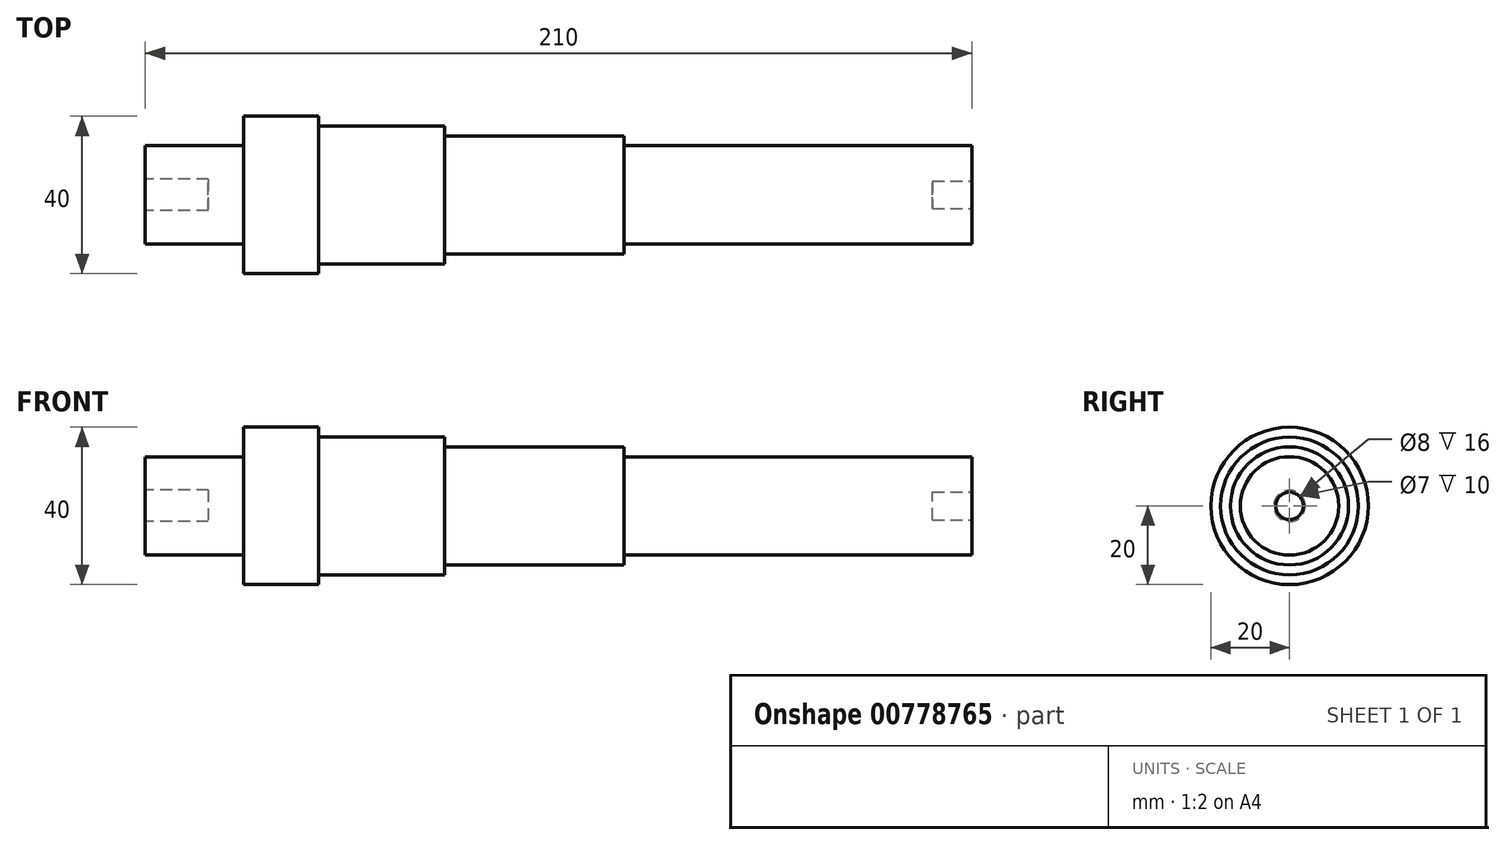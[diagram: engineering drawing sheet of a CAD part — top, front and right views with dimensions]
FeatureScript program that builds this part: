
annotation { "Feature Type Name" : "Feature", "Feature Type Description" : "" }
export const myFeature = defineFeature(function(context is Context, id is Id, definition is map)
    precondition{}
    {
        {
            var Q0;
            Q0=qCreatedBy(makeId("Front.planeOp"),FACE);
            var sketch = newSketch(context, id + "F0", { "sketchPlane" : qUnion([Q0])});
            skLineSegment(sketch, "E0", {"start": v(-5.4, 0) * mm, "end": v(218.84, 0) * mm, "construction": true});
            skLineSegment(sketch, "E1", {"start": v(0, 0) * mm, "end": v(0, 12.5) * mm});
            skLineSegment(sketch, "E2", {"start": v(0, 12.5) * mm, "end": v(25, 12.5) * mm});
            skLineSegment(sketch, "E3", {"start": v(25, 12.5) * mm, "end": v(25, 20) * mm});
            skLineSegment(sketch, "E4", {"start": v(25, 20) * mm, "end": v(44, 20) * mm});
            skLineSegment(sketch, "E5", {"start": v(44, 20) * mm, "end": v(44, 17.5) * mm});
            skLineSegment(sketch, "E6", {"start": v(44, 17.5) * mm, "end": v(76, 17.5) * mm});
            skLineSegment(sketch, "E7", {"start": v(76, 17.5) * mm, "end": v(76, 15) * mm});
            skLineSegment(sketch, "E8", {"start": v(76, 15) * mm, "end": v(121.6, 15) * mm});
            skLineSegment(sketch, "E9", {"start": v(121.6, 15) * mm, "end": v(121.6, 12.5) * mm});
            skLineSegment(sketch, "E10", {"start": v(121.6, 12.5) * mm, "end": v(210, 12.5) * mm});
            skLineSegment(sketch, "E11", {"start": v(210, 12.5) * mm, "end": v(210, 0) * mm});
            skLineSegment(sketch, "E12", {"start": v(0, 0) * mm, "end": v(210, 0) * mm});
            skSolve(sketch);
        }
        {
            var Q0;
            Q0 = qSketchRegion(id + "F0", true);
            var Q1;
            Q1=sQuery(id+"F0.wireOp",EDGE,"E0");
            revolve(context, id + "F1", {"surfaceOperationType" : NewSurfaceOperationType.NEW, "entities" : qUnion([Q0]), "axis" : qUnion([Q1]), "revolveType" : RevolveType.FULL});
        }
        {
            var Q0;
            Q0=makeQuery(id+"F1.opRevolve","SWEPT_FACE",FACE,{"disambiguationData":[OSD([sQuery(id+"F0.wireOp",EDGE,"E1")])]});
            var sketch = newSketch(context, id + "F2", { "sketchPlane" : qUnion([Q0])});
            skCircle(sketch, "E13", {"center": v(0, 0) * mm, "radius": 4 * mm});
            skSolve(sketch);
        }
        {
            var Q0;
            Q0 = qSketchRegion(id + "F2", true);
            extrude(context, id + "F3", {"entities" : qUnion([Q0]), "operationType" : NewBodyOperationType.REMOVE, "oppositeDirection" : true, "depth" : 16 * mm, "offsetDistance" : 25 * mm});
        }
        {
            var Q0;
            Q0=makeQuery(id+"F1.opRevolve","SWEPT_FACE",FACE,{"disambiguationData":[OSD([sQuery(id+"F0.wireOp",EDGE,"E11")])]});
            var sketch = newSketch(context, id + "F4", { "sketchPlane" : qUnion([Q0])});
            skCircle(sketch, "E14", {"center": v(0, 0) * mm, "radius": 3.5 * mm});
            skSolve(sketch);
        }
        {
            var Q0;
            Q0 = qSketchRegion(id + "F4", true);
            extrude(context, id + "F5", {"entities" : qUnion([Q0]), "operationType" : NewBodyOperationType.REMOVE, "oppositeDirection" : true, "depth" : 10 * mm, "offsetDistance" : 25 * mm});
        }
    });
